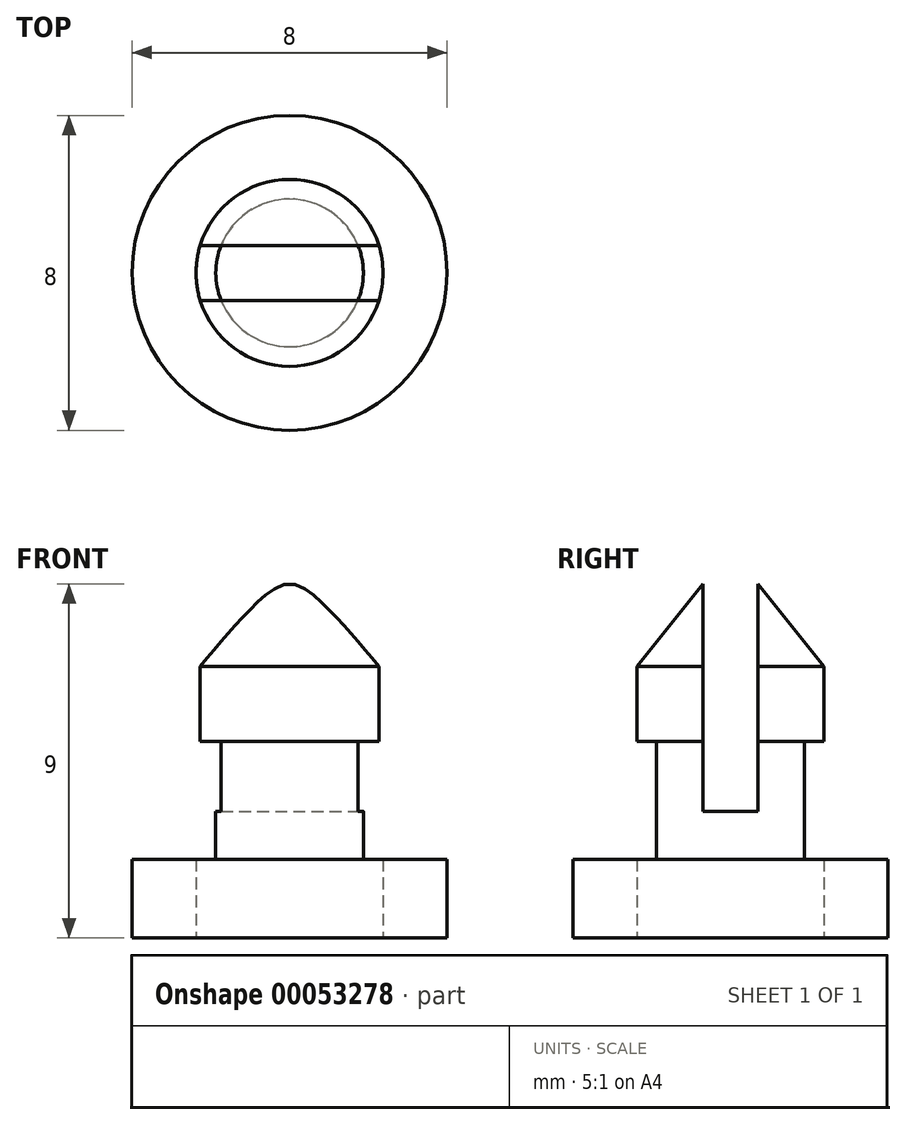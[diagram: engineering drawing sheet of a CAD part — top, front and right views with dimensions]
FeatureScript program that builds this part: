
annotation { "Feature Type Name" : "Feature", "Feature Type Description" : "" }
export const myFeature = defineFeature(function(context is Context, id is Id, definition is map)
    precondition{}
    {
        {
            var Q0;
            Q0=qCreatedBy(makeId("Top.planeOp"),FACE);
            var sketch = newSketch(context, id + "F0", { "sketchPlane" : qUnion([Q0])});
            skCircle(sketch, "E0", {"center": v(0, 0) * mm, "radius": 4 * mm});
            skSolve(sketch);
        }
        {
            var Q0;
            Q0 = qSketchRegion(id + "F0", true);
            extrude(context, id + "F1", {"entities" : qUnion([Q0]), "depth" : 2 * mm});
        }
        {
            var Q0;
            Q0=qCreatedBy(makeId("Top.planeOp"),FACE);
            var sketch = newSketch(context, id + "F2", { "sketchPlane" : qUnion([Q0])});
            skCircle(sketch, "E1", {"center": v(0, 0) * mm, "radius": 2.38 * mm});
            skSolve(sketch);
        }
        {
            var Q0;
            Q0=makeQuery(id+"F2.imprint","IMPRINT",FACE,{"disambiguationData":[TD([[makeQuery(id+"F2.imprint","IMPRINT",EDGE,{"derivedFrom":sQuery(id+"F2.wireOp",EDGE,"E1")}),1.0]])]});
            var Q1;
            Q1=sQuery(id+"F2.wireOp",EDGE,"E1");
            extrude(context, id + "F3", {"entities" : qUnion([Q0]), "surfaceEntities" : qUnion([Q1]), "depth" : 9 * mm});
        }
        {
            var Q0;
            Q0=qCreatedBy(makeId("Front.planeOp"),FACE);
            var sketch = newSketch(context, id + "F4", { "sketchPlane" : qUnion([Q0])});
            skLineSegment(sketch, "E2.bottom", {"start": v(-3.88, 5) * mm, "end": v(-1.88, 5) * mm});
            skLineSegment(sketch, "E2.top", {"start": v(-3.88, 2) * mm, "end": v(-1.88, 2) * mm});
            skLineSegment(sketch, "E2.left", {"start": v(-3.88, 5) * mm, "end": v(-3.88, 2) * mm});
            skLineSegment(sketch, "E2.right", {"start": v(-1.88, 5) * mm, "end": v(-1.88, 2) * mm});
            skSolve(sketch);
        }
        {
            var Q0;
            Q0=qCreatedBy(makeId("Front.planeOp"),FACE);
            var sketch = newSketch(context, id + "F5", { "sketchPlane" : qUnion([Q0])});
            skLineSegment(sketch, "E3", {"start": v(0, 0) * mm, "end": v(0, 11.67) * mm});
            skSolve(sketch);
        }
        {
            var Q0;
            Q0=makeQuery(id+"F4.imprint","IMPRINT",FACE,{"disambiguationData":[TD([[makeQuery(id+"F4.imprint","IMPRINT",EDGE,{"derivedFrom":sQuery(id+"F4.wireOp",EDGE,"E2.bottom")}),-1.0]])]});
            var Q1;
            Q1=sQuery(id+"F5.wireOp",EDGE,"E3");
            revolve(context, id + "F6", {"operationType" : NewBodyOperationType.REMOVE, "entities" : qUnion([Q0]), "axis" : qUnion([Q1]), "revolveType" : RevolveType.FULL, "oppositeDirection" : true});
        }
        {
            var Q0;
            Q0=qCreatedBy(makeId("Front.planeOp"),FACE);
            var sketch = newSketch(context, id + "F7", { "sketchPlane" : qUnion([Q0])});
            skLineSegment(sketch, "E4", {"start": v(-0.5, 9.25) * mm, "end": v(-2.5, 6.75) * mm});
            skLineSegment(sketch, "E5", {"start": v(-2.5, 6.75) * mm, "end": v(-2.5, 9.25) * mm});
            skLineSegment(sketch, "E6", {"start": v(-2.5, 9.25) * mm, "end": v(-0.5, 9.25) * mm});
            skSolve(sketch);
        }
        {
            var Q0;
            Q0=qCreatedBy(makeId("Front.planeOp"),FACE);
            var sketch = newSketch(context, id + "F8", { "sketchPlane" : qUnion([Q0])});
            skLineSegment(sketch, "E7", {"start": v(0, -3.26) * mm, "end": v(0, 12.16) * mm});
            skSolve(sketch);
        }
        {
            var Q0;
            Q0 = qSketchRegion(id + "F7", true);
            var Q1;
            Q1=sQuery(id+"F8.wireOp",EDGE,"E7");
            revolve(context, id + "F9", {"operationType" : NewBodyOperationType.REMOVE, "entities" : qUnion([Q0]), "axis" : qUnion([Q1]), "revolveType" : RevolveType.FULL, "oppositeDirection" : true});
        }
        {
            var Q0;
            Q0=qCreatedBy(makeId("Right.planeOp"),FACE);
            var sketch = newSketch(context, id + "F10", { "sketchPlane" : qUnion([Q0])});
            skLineSegment(sketch, "E8.bottom", {"start": v(-0.7, 9.72) * mm, "end": v(0.7, 9.72) * mm});
            skLineSegment(sketch, "E8.top", {"start": v(-0.7, 3.22) * mm, "end": v(0.7, 3.22) * mm});
            skLineSegment(sketch, "E8.left", {"start": v(-0.7, 9.72) * mm, "end": v(-0.7, 3.22) * mm});
            skLineSegment(sketch, "E8.right", {"start": v(0.7, 9.72) * mm, "end": v(0.7, 3.22) * mm});
            skSolve(sketch);
        }
        {
            var Q0;
            Q0 = qSketchRegion(id + "F10", true);
            extrude(context, id + "F11", {"entities" : qUnion([Q0]), "operationType" : NewBodyOperationType.REMOVE, "endBound" : BoundingType.SYMMETRIC, "oppositeDirection" : true, "depth" : 5 * mm});
        }
    });
